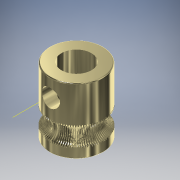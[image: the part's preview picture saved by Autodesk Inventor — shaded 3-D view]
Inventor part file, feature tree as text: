
AUTODESK INVENTOR PART (.ipt)
format: ipt  version: 2018 (Build 220112000, 112)  size: 1,610,240 bytes
history: native  units: mm
features: sketch x5, extrude x2, revolve x2, fillet x1, plane x1, other x1, pattern_circular x1
ambient origin geometry x8: Origin, YZ Plane, XZ Plane, XY Plane, X Axis, Y Axis, Z Axis, Center Point
bodies: Solid1 (feature_tree)
feature tree (13):
  extrude  "Extrusion1"  Depth=5.0mm
  revolve  "Revolution1"  [1 undecoded]
  extrude  "Extrusion2"  Depth=3.5mm
  fillet  "Fillet1"  [1 undecoded]
  plane  "Work Plane1"
  sketch  "Sketch4"  dims[d8=3.0mm d9=3.0mm]
  other  "Work Axis1"
  revolve  "Revolution2"  [1 undecoded]
  pattern_circular  "Circular Pattern1"  [2 undecoded]
  sketch  "Sketch1"  dims[d0=9.0mm d1=5.0mm]
  sketch  "Sketch2"  dims[d2=11.0mm d3=0.0mm d4=3.25mm]
  sketch  "Sketch3"  dims[d5=3.0mm d6=3.5mm d7=90.0deg]
  sketch  "Sketch5"  dims[d10=11.0mm d11=0.0mm d12=0.2mm d13=-3.25mm d14=0.05mm d15=0.3mm d16=0.2mm d17=0.4mm d18=90.0deg d19=900.0mm d20=360.0deg]
note: 5 required parameter values undecoded (feature->parameter linkage not recoverable at this tier; creation-order binding heuristic only, values carry confidence <= 0.55)